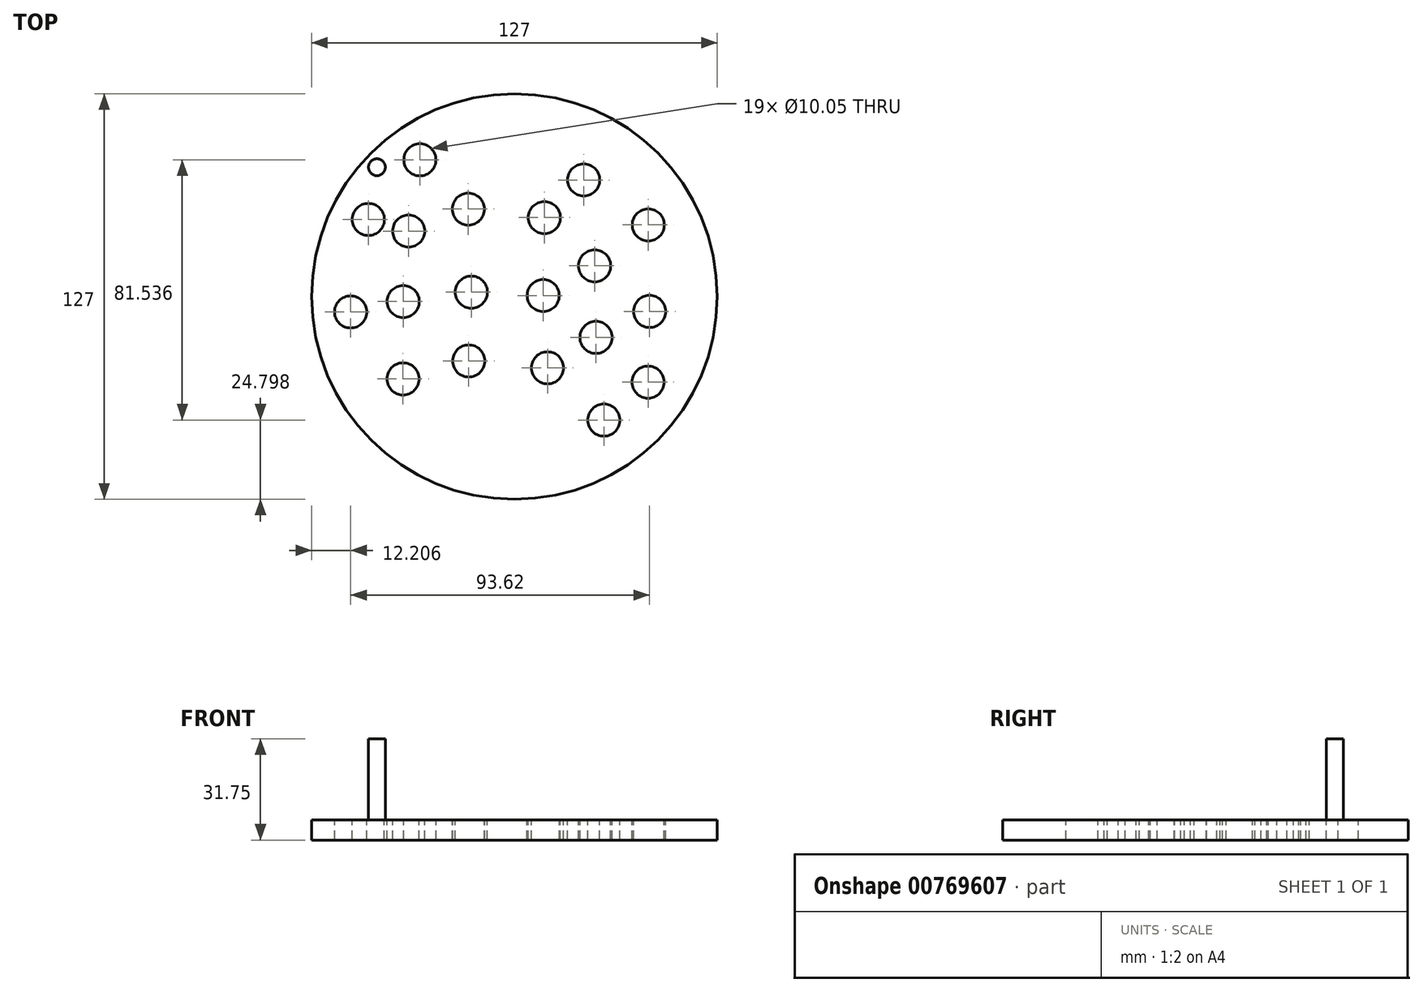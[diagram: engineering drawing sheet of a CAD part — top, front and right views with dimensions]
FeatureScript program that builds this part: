
annotation { "Feature Type Name" : "Feature", "Feature Type Description" : "" }
export const myFeature = defineFeature(function(context is Context, id is Id, definition is map)
    precondition{}
    {
        {
            var Q0;
            Q0=qCreatedBy(makeId("Top.planeOp"),FACE);
            var sketch = newSketch(context, id + "F0", { "sketchPlane" : qUnion([Q0])});
            skCircle(sketch, "E0", {"center": v(0, 0) * mm, "radius": 63.5 * mm});
            skSolve(sketch);
        }
        {
            var Q0;
            Q0=makeQuery(id+"F0.imprint","IMPRINT",FACE,{"disambiguationData":[TD([[makeQuery(id+"F0.imprint","IMPRINT",EDGE,{"derivedFrom":sQuery(id+"F0.wireOp",EDGE,"E0")}),1.0]])]});
            extrude(context, id + "F1", {"entities" : qUnion([Q0]), "depth" : 6.35 * mm, "offsetDistance" : 25.4 * mm});
        }
        {
            var Q0;
            Q0=makeQuery(id+"F1.opExtrude","CAP_FACE",FACE,{"disambiguationData":[OSD([sQuery(id+"F0.wireOp",EDGE,"E0")])],"isStart":false});
            var sketch = newSketch(context, id + "F2", { "sketchPlane" : qUnion([Q0])});
            skCircle(sketch, "E1", {"center": v(-29.61, 42.83) * mm, "radius": 5.03 * mm});
            skCircle(sketch, "E2", {"center": v(-33.12, 20.5) * mm, "radius": 5.03 * mm});
            skCircle(sketch, "E3", {"center": v(-34.82, -1.57) * mm, "radius": 5.03 * mm});
            skCircle(sketch, "E4", {"center": v(-34.88, -25.81) * mm, "radius": 5.03 * mm});
            skCircle(sketch, "E5", {"center": v(-14.44, 27.38) * mm, "radius": 5.03 * mm});
            skCircle(sketch, "E6", {"center": v(-13.49, 1.38) * mm, "radius": 5.03 * mm});
            skCircle(sketch, "E7", {"center": v(-14.31, -20.18) * mm, "radius": 5.03 * mm});
            skCircle(sketch, "E8", {"center": v(-51.3, -4.83) * mm, "radius": 5.03 * mm});
            skCircle(sketch, "E9", {"center": v(-45.76, 24.14) * mm, "radius": 5.03 * mm});
            skCircle(sketch, "E10", {"center": v(10.36, -22.34) * mm, "radius": 5.03 * mm});
            skCircle(sketch, "E11", {"center": v(9, 0.3) * mm, "radius": 5.03 * mm});
            skCircle(sketch, "E12", {"center": v(9.35, 24.72) * mm, "radius": 5.03 * mm});
            skCircle(sketch, "E13", {"center": v(21.67, 36.52) * mm, "radius": 5.03 * mm});
            skCircle(sketch, "E14", {"center": v(25.1, 9.6) * mm, "radius": 5.03 * mm});
            skCircle(sketch, "E15", {"center": v(25.54, -12.8) * mm, "radius": 5.03 * mm});
            skCircle(sketch, "E16", {"center": v(28, -38.7) * mm, "radius": 5.03 * mm});
            skCircle(sketch, "E17", {"center": v(42.33, -4.66) * mm, "radius": 5.03 * mm});
            skCircle(sketch, "E18", {"center": v(41.91, 22.43) * mm, "radius": 5.03 * mm});
            skCircle(sketch, "E19", {"center": v(41.84, -26.81) * mm, "radius": 5.03 * mm});
            skSolve(sketch);
        }
        {
            var Q0;
            Q0=makeQuery(id+"F2.imprint","IMPRINT",FACE,{"disambiguationData":[TD([[makeQuery(id+"F2.imprint","IMPRINT",EDGE,{"derivedFrom":sQuery(id+"F2.wireOp",EDGE,"E8")}),1.0]])]});
            var Q1;
            Q1=makeQuery(id+"F2.imprint","IMPRINT",FACE,{"disambiguationData":[TD([[makeQuery(id+"F2.imprint","IMPRINT",EDGE,{"derivedFrom":sQuery(id+"F2.wireOp",EDGE,"E9")}),1.0]])]});
            var Q2;
            Q2=makeQuery(id+"F2.imprint","IMPRINT",FACE,{"disambiguationData":[TD([[makeQuery(id+"F2.imprint","IMPRINT",EDGE,{"derivedFrom":sQuery(id+"F2.wireOp",EDGE,"E1")}),1.0]])]});
            var Q3;
            Q3=makeQuery(id+"F2.imprint","IMPRINT",FACE,{"disambiguationData":[TD([[makeQuery(id+"F2.imprint","IMPRINT",EDGE,{"derivedFrom":sQuery(id+"F2.wireOp",EDGE,"E2")}),1.0]])]});
            var Q4;
            Q4=makeQuery(id+"F2.imprint","IMPRINT",FACE,{"disambiguationData":[TD([[makeQuery(id+"F2.imprint","IMPRINT",EDGE,{"derivedFrom":sQuery(id+"F2.wireOp",EDGE,"E3")}),1.0]])]});
            var Q5;
            Q5=makeQuery(id+"F2.imprint","IMPRINT",FACE,{"disambiguationData":[TD([[makeQuery(id+"F2.imprint","IMPRINT",EDGE,{"derivedFrom":sQuery(id+"F2.wireOp",EDGE,"E4")}),1.0]])]});
            var Q6;
            Q6=makeQuery(id+"F2.imprint","IMPRINT",FACE,{"disambiguationData":[TD([[makeQuery(id+"F2.imprint","IMPRINT",EDGE,{"derivedFrom":sQuery(id+"F2.wireOp",EDGE,"E7")}),1.0]])]});
            var Q7;
            Q7=makeQuery(id+"F2.imprint","IMPRINT",FACE,{"disambiguationData":[TD([[makeQuery(id+"F2.imprint","IMPRINT",EDGE,{"derivedFrom":sQuery(id+"F2.wireOp",EDGE,"E6")}),1.0]])]});
            var Q8;
            Q8=makeQuery(id+"F2.imprint","IMPRINT",FACE,{"disambiguationData":[TD([[makeQuery(id+"F2.imprint","IMPRINT",EDGE,{"derivedFrom":sQuery(id+"F2.wireOp",EDGE,"E5")}),1.0]])]});
            var Q9;
            Q9=makeQuery(id+"F2.imprint","IMPRINT",FACE,{"disambiguationData":[TD([[makeQuery(id+"F2.imprint","IMPRINT",EDGE,{"derivedFrom":sQuery(id+"F2.wireOp",EDGE,"E13")}),1.0]])]});
            var Q10;
            Q10=makeQuery(id+"F2.imprint","IMPRINT",FACE,{"disambiguationData":[TD([[makeQuery(id+"F2.imprint","IMPRINT",EDGE,{"derivedFrom":sQuery(id+"F2.wireOp",EDGE,"E12")}),1.0]])]});
            var Q11;
            Q11=makeQuery(id+"F2.imprint","IMPRINT",FACE,{"disambiguationData":[TD([[makeQuery(id+"F2.imprint","IMPRINT",EDGE,{"derivedFrom":sQuery(id+"F2.wireOp",EDGE,"E11")}),1.0]])]});
            var Q12;
            Q12=makeQuery(id+"F2.imprint","IMPRINT",FACE,{"disambiguationData":[TD([[makeQuery(id+"F2.imprint","IMPRINT",EDGE,{"derivedFrom":sQuery(id+"F2.wireOp",EDGE,"E10")}),1.0]])]});
            var Q13;
            Q13=makeQuery(id+"F2.imprint","IMPRINT",FACE,{"disambiguationData":[TD([[makeQuery(id+"F2.imprint","IMPRINT",EDGE,{"derivedFrom":sQuery(id+"F2.wireOp",EDGE,"E16")}),1.0]])]});
            var Q14;
            Q14=makeQuery(id+"F2.imprint","IMPRINT",FACE,{"disambiguationData":[TD([[makeQuery(id+"F2.imprint","IMPRINT",EDGE,{"derivedFrom":sQuery(id+"F2.wireOp",EDGE,"E15")}),1.0]])]});
            var Q15;
            Q15=makeQuery(id+"F2.imprint","IMPRINT",FACE,{"disambiguationData":[TD([[makeQuery(id+"F2.imprint","IMPRINT",EDGE,{"derivedFrom":sQuery(id+"F2.wireOp",EDGE,"E14")}),1.0]])]});
            var Q16;
            Q16=makeQuery(id+"F2.imprint","IMPRINT",FACE,{"disambiguationData":[TD([[makeQuery(id+"F2.imprint","IMPRINT",EDGE,{"derivedFrom":sQuery(id+"F2.wireOp",EDGE,"E18")}),1.0]])]});
            var Q17;
            Q17=makeQuery(id+"F2.imprint","IMPRINT",FACE,{"disambiguationData":[TD([[makeQuery(id+"F2.imprint","IMPRINT",EDGE,{"derivedFrom":sQuery(id+"F2.wireOp",EDGE,"E17")}),1.0]])]});
            var Q18;
            Q18=makeQuery(id+"F2.imprint","IMPRINT",FACE,{"disambiguationData":[TD([[makeQuery(id+"F2.imprint","IMPRINT",EDGE,{"derivedFrom":sQuery(id+"F2.wireOp",EDGE,"E19")}),1.0]])]});
            var Q19;
            Q19 = qConstructionFilter(qBodyType(qCreatedBy(id + "F2" ,EDGE), BodyType.WIRE), ConstructionObject.NO);
            extrude(context, id + "F3", {"entities" : qUnion([Q0, Q1, Q2, Q3, Q4, Q5, Q6, Q7, Q8, Q9, Q10, Q11, Q12, Q13, Q14, Q15, Q16, Q17, Q18]), "operationType" : NewBodyOperationType.REMOVE, "surfaceEntities" : qUnion([Q19]), "oppositeDirection" : true, "depth" : 25.4 * mm, "offsetDistance" : 25.4 * mm});
        }
        {
            var Q0;
            Q0=makeQuery(id+"F1.opExtrude","CAP_FACE",FACE,{"disambiguationData":[OSD([sQuery(id+"F0.wireOp",EDGE,"E0")])],"isStart":false});
            var sketch = newSketch(context, id + "F4", { "sketchPlane" : qUnion([Q0])});
            skCircle(sketch, "E20", {"center": v(-43.08, 40.5) * mm, "radius": 2.64 * mm});
            skSolve(sketch);
        }
        {
            var Q0;
            Q0=makeQuery(id+"F4.imprint","IMPRINT",FACE,{"disambiguationData":[TD([[makeQuery(id+"F4.imprint","IMPRINT",EDGE,{"derivedFrom":sQuery(id+"F4.wireOp",EDGE,"E20")}),1.0]])]});
            extrude(context, id + "F5", {"entities" : qUnion([Q0]), "operationType" : NewBodyOperationType.ADD, "depth" : 25.4 * mm, "offsetDistance" : 25.4 * mm});
        }
        {
            var Q0;
            Q0=makeQuery(id+"F1.opExtrude","CAP_FACE",FACE,{"disambiguationData":[OSD([sQuery(id+"F0.wireOp",EDGE,"E0")])],"isStart":false});
            var sketch = newSketch(context, id + "F6", { "sketchPlane" : qUnion([Q0])});
            skCircle(sketch, "E21", {"center": v(38.78, 41.23) * mm, "radius": 2.64 * mm});
            skCircle(sketch, "E22", {"center": v(42.67, -38.63) * mm, "radius": 2.64 * mm});
            skCircle(sketch, "E23", {"center": v(-46.87, -33.76) * mm, "radius": 2.64 * mm});
            skSolve(sketch);
        }
        {
            var Q0;
            Q0=sQuery(id+"F6.wireOp",EDGE,"E21");
            var Q1;
            Q1=sQuery(id+"F6.wireOp",EDGE,"E22");
            var Q2;
            Q2=sQuery(id+"F6.wireOp",EDGE,"E23");
            extrude(context, id + "F7", {"bodyType" : ToolBodyType.SURFACE, "surfaceEntities" : qUnion([Q0, Q1, Q2]), "depth" : 25.4 * mm, "offsetDistance" : 25.4 * mm});
        }
    });
